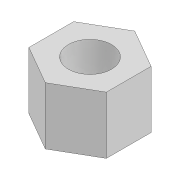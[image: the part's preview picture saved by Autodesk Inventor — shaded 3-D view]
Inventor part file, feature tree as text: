
AUTODESK INVENTOR PART (.ipt)
format: ipt  version: 2022 (Build 260153000, 153)  size: 88,064 bytes
history: native  units: mm
features: extrude x2, sketch x2
ambient origin geometry x8: Origin, YZ Plane, XZ Plane, XY Plane, X Axis, Y Axis, Z Axis, Center Point
bodies: Solid1 (feature_tree)
feature tree (4):
  extrude  "Extrusion1"  Depth=4.0mm TaperAngle=0.0deg
  extrude  "Extrusion2"  Depth=4.0mm TaperAngle=0.0deg
  sketch  "Sketch1"  dims[d0=5.4mm d1=4.0mm d2=0.0mm]
  sketch  "Sketch2"  dims[d3=3.0mm d4=4.0mm d5=0.0mm]
